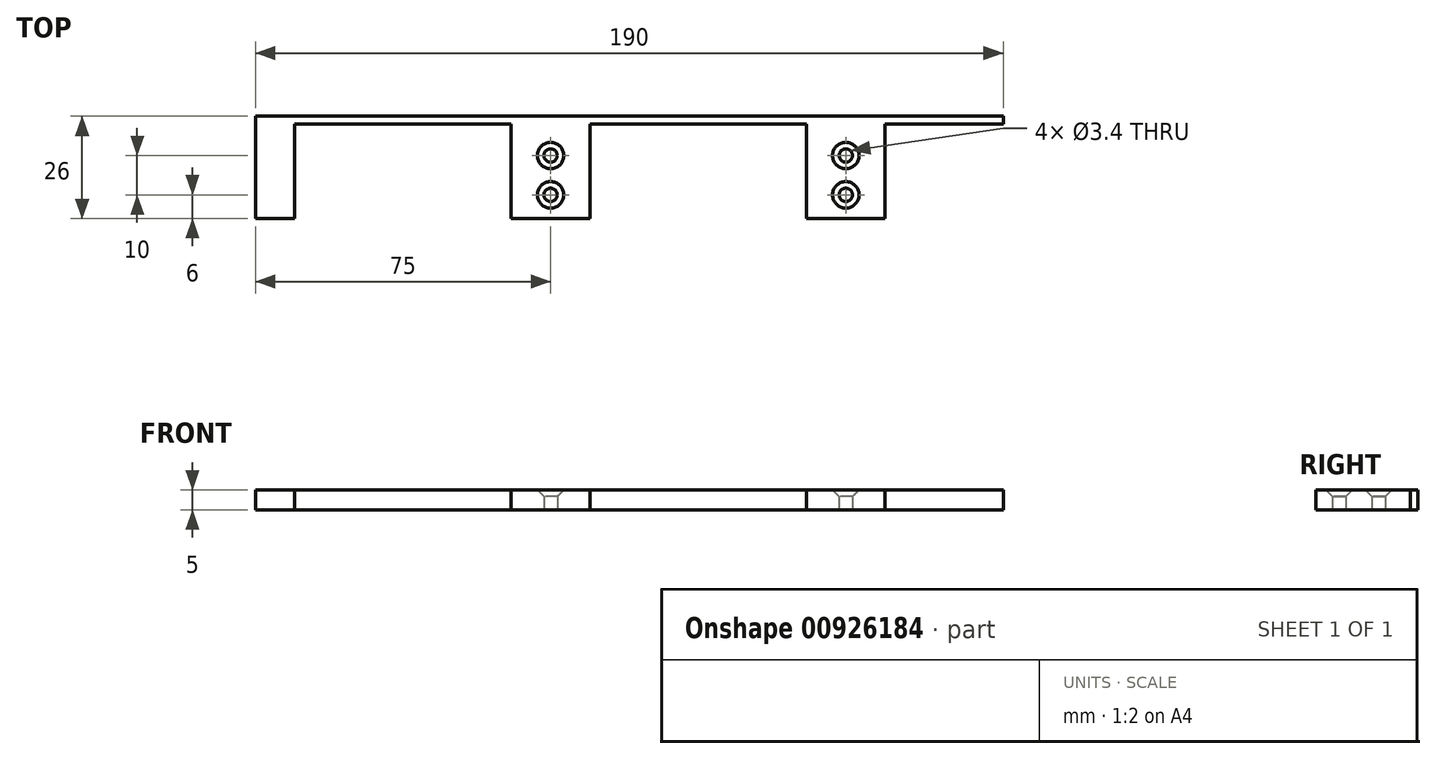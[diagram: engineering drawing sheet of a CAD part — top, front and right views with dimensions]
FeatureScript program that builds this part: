
annotation { "Feature Type Name" : "Feature", "Feature Type Description" : "" }
export const myFeature = defineFeature(function(context is Context, id is Id, definition is map)
    precondition{}
    {
        {
            var Q0;
            Q0=qCreatedBy(makeId("Top.planeOp"),FACE);
            var sketch = newSketch(context, id + "F0", { "sketchPlane" : qUnion([Q0])});
            skCircle(sketch, "E0", {"center": v(-20, 3) * mm, "radius": 1.7 * mm});
            skCircle(sketch, "E1", {"center": v(55, -7) * mm, "radius": 1.7 * mm});
            skCircle(sketch, "E2", {"center": v(55, 3) * mm, "radius": 1.7 * mm});
            skCircle(sketch, "E3", {"center": v(-20, -7) * mm, "radius": 1.7 * mm});
            skLineSegment(sketch, "E4", {"start": v(-95, 13) * mm, "end": v(-95, -13) * mm});
            skLineSegment(sketch, "E5", {"start": v(95, 11) * mm, "end": v(95, 13) * mm});
            skLineSegment(sketch, "E6", {"start": v(95, 11) * mm, "end": v(65, 11) * mm});
            skLineSegment(sketch, "E7", {"start": v(45, -13) * mm, "end": v(45, 3) * mm});
            skLineSegment(sketch, "E8", {"start": v(-30, -13) * mm, "end": v(-10, -13) * mm});
            skLineSegment(sketch, "E9", {"start": v(-30, -13) * mm, "end": v(-30, 3) * mm});
            skLineSegment(sketch, "E10", {"start": v(95, 13) * mm, "end": v(-95, 13) * mm});
            skLineSegment(sketch, "E11", {"start": v(-95, -13) * mm, "end": v(-85, -13) * mm});
            skLineSegment(sketch, "E12", {"start": v(45, -13) * mm, "end": v(65, -13) * mm});
            skLineSegment(sketch, "E13", {"start": v(-30, -13) * mm, "end": v(-30, 11) * mm});
            skLineSegment(sketch, "E14", {"start": v(-30, 11) * mm, "end": v(-85, 11) * mm});
            skLineSegment(sketch, "E15", {"start": v(-85, 11) * mm, "end": v(-85, -13) * mm});
            skLineSegment(sketch, "E16", {"start": v(45, -13) * mm, "end": v(45, 11) * mm});
            skLineSegment(sketch, "E17", {"start": v(45, 11) * mm, "end": v(-10, 11) * mm});
            skLineSegment(sketch, "E18", {"start": v(-10, 11) * mm, "end": v(-10, -13) * mm});
            skLineSegment(sketch, "E19", {"start": v(65, 11) * mm, "end": v(65, -13) * mm});
            skSolve(sketch);
        }
        {
            var Q0;
            Q0 = qSketchRegion(id + "F0", true);
            extrude(context, id + "F1", {"entities" : qUnion([Q0]), "depth" : 5 * mm, "offsetDistance" : 25 * mm});
        }
        {
            var Q0;
            Q0=makeQuery(id+"F1.opExtrude","CAP_FACE",FACE,{"disambiguationData":[OSD([sQuery(id+"F0.wireOp",EDGE,"E0"),sQuery(id+"F0.wireOp",EDGE,"E1"),sQuery(id+"F0.wireOp",EDGE,"E2"),sQuery(id+"F0.wireOp",EDGE,"E3"),sQuery(id+"F0.wireOp",EDGE,"E4"),sQuery(id+"F0.wireOp",EDGE,"E5"),sQuery(id+"F0.wireOp",EDGE,"E8"),sQuery(id+"F0.wireOp",EDGE,"E10"),sQuery(id+"F0.wireOp",EDGE,"E11"),sQuery(id+"F0.wireOp",EDGE,"E12"),sQuery(id+"F0.wireOp",EDGE,"E13"),sQuery(id+"F0.wireOp",EDGE,"E14"),sQuery(id+"F0.wireOp",EDGE,"E15"),sQuery(id+"F0.wireOp",EDGE,"E16"),sQuery(id+"F0.wireOp",EDGE,"E17"),sQuery(id+"F0.wireOp",EDGE,"E18"),sQuery(id+"F0.wireOp",EDGE,"E6"),sQuery(id+"F0.wireOp",EDGE,"E19")])],"isStart":false});
            var sketch = newSketch(context, id + "F2", { "sketchPlane" : qUnion([Q0])});
            skPoint(sketch, "E20", {"position": v(-20, 3) * mm});
            skPoint(sketch, "E21", {"position": v(-20, -7) * mm});
            skPoint(sketch, "E22", {"position": v(55, 3) * mm});
            skPoint(sketch, "E23", {"position": v(55, -7) * mm});
            skSolve(sketch);
        }
        {
            var Q0;
            Q0=sQuery(id+"F2.wireOp",VERTEX,"E20");
            var Q1;
            Q1=sQuery(id+"F2.wireOp",VERTEX,"E21");
            var Q2;
            Q2=sQuery(id+"F2.wireOp",VERTEX,"E22");
            var Q3;
            Q3=sQuery(id+"F2.wireOp",VERTEX,"E23");
            var Q4;
            Q4=makeQuery(id+"F1.opExtrude","SWEPT_BODY",BODY,{"disambiguationData":[OSD([sQuery(id+"F0.wireOp",EDGE,"E0"),sQuery(id+"F0.wireOp",EDGE,"E1"),sQuery(id+"F0.wireOp",EDGE,"E2"),sQuery(id+"F0.wireOp",EDGE,"E3"),sQuery(id+"F0.wireOp",EDGE,"E4"),sQuery(id+"F0.wireOp",EDGE,"E5"),sQuery(id+"F0.wireOp",EDGE,"E8"),sQuery(id+"F0.wireOp",EDGE,"E10"),sQuery(id+"F0.wireOp",EDGE,"E11"),sQuery(id+"F0.wireOp",EDGE,"E12"),sQuery(id+"F0.wireOp",EDGE,"E13"),sQuery(id+"F0.wireOp",EDGE,"E14"),sQuery(id+"F0.wireOp",EDGE,"E15"),sQuery(id+"F0.wireOp",EDGE,"E16"),sQuery(id+"F0.wireOp",EDGE,"E17"),sQuery(id+"F0.wireOp",EDGE,"E18"),sQuery(id+"F0.wireOp",EDGE,"E6"),sQuery(id+"F0.wireOp",EDGE,"E19")])]});
            hole(context, id + "F3", {"style" : HoleStyle.C_SINK, "endStyle" : HoleEndStyle.THROUGH, "standardTappedOrClearance" : lookupTablePath({ "fit" : "Normal", "standard" : "ISO", "size" : "M3", "type" : "Clearance" }), "standardBlindInLast" : lookupTablePath({ "fit" : "Normal", "standard" : "ISO", "size" : "M3", "type" : "Clearance" }), "holeDiameter" : 3.4 * mm, "cSinkDiameter" : 6.72 * mm, "cSinkAngle" : 90 * degree, "majorDiameter" : 5 * mm, "isTappedThrough" : true, "tappedDepth" : 12 * mm, "tapClearance" : 3, "locations" : qUnion([Q0, Q1, Q2, Q3]), "scope" : qUnion([Q4])});
        }
    });
